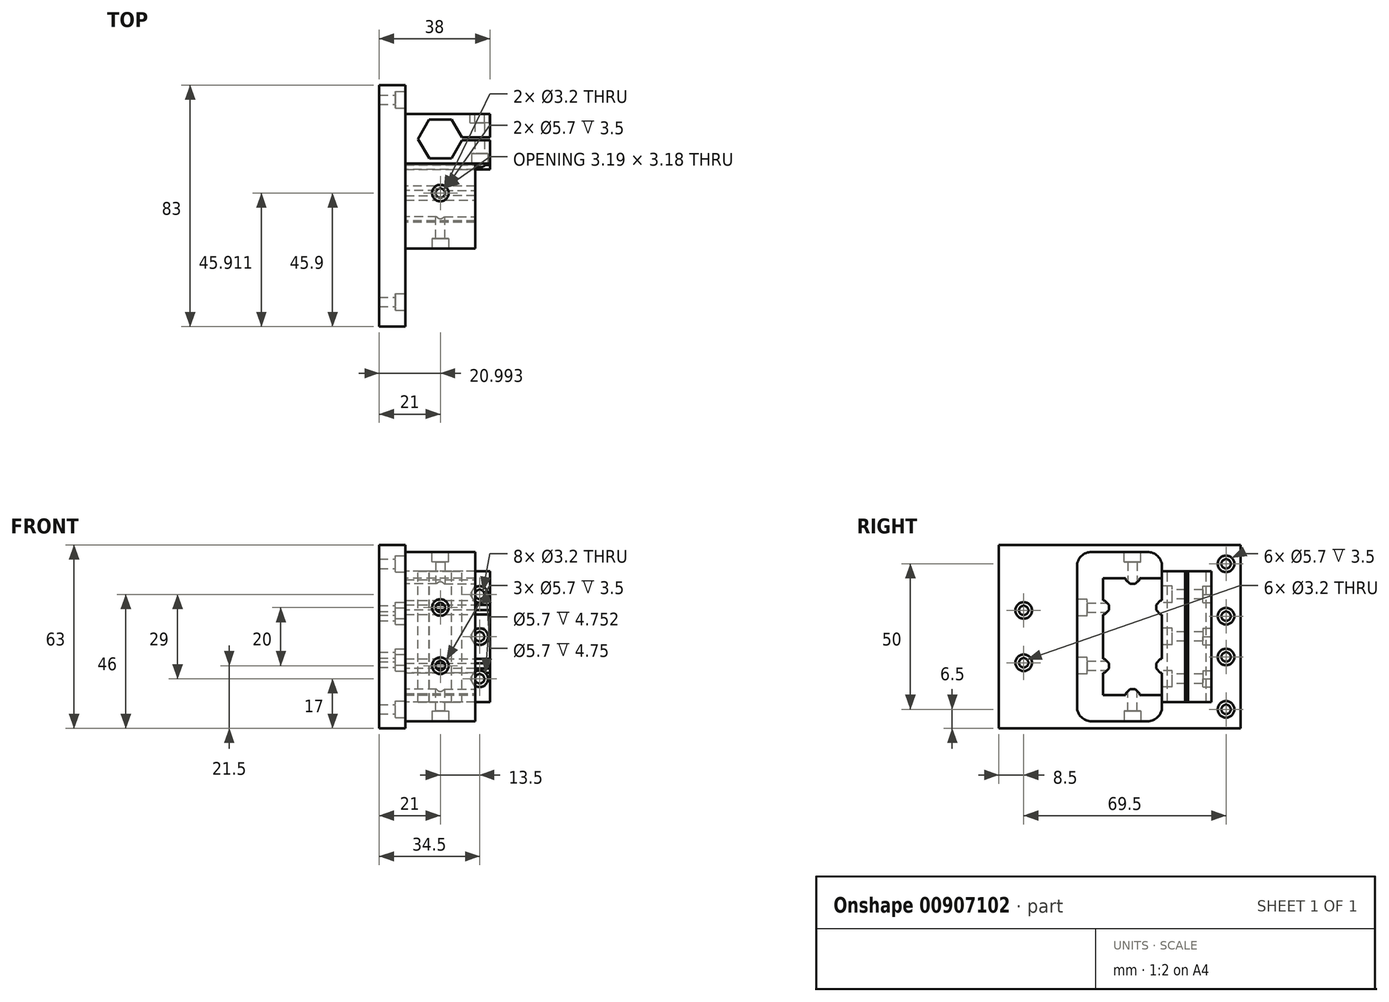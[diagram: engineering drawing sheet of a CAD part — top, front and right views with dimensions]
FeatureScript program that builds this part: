
annotation { "Feature Type Name" : "Feature", "Feature Type Description" : "" }
export const myFeature = defineFeature(function(context is Context, id is Id, definition is map)
    precondition{}
    {
        {
            assignVariable(context, id + "F0", {"name" : "headdepth", "anyValue" : 3.5 * mm});
        }
        {
            assignVariable(context, id + "F1", {"name" : "nutdepth", "anyValue" : 3});
        }
        {
            var Q0;
            Q0=qCreatedBy(makeId("Top.planeOp"),FACE);
            var sketch = newSketch(context, id + "F2", { "sketchPlane" : qUnion([Q0])});
            skLineSegment(sketch, "E0.bottom", {"start": v(0, 0) * mm, "end": v(9, 0) * mm});
            skLineSegment(sketch, "E0.top", {"start": v(0, 83) * mm, "end": v(9, 83) * mm});
            skLineSegment(sketch, "E0.left", {"start": v(0, 0) * mm, "end": v(0, 83) * mm});
            skLineSegment(sketch, "E0.right", {"start": v(9, 0) * mm, "end": v(9, 83) * mm});
            skSolve(sketch);
        }
        {
            var Q0;
            Q0 = qSketchRegion(id + "F2", true);
            var Q1;
            Q1=makeQuery(id+"F2.imprint","IMPRINT",FACE,{"disambiguationData":[TD([[makeQuery(id+"F2.imprint","IMPRINT",EDGE,{"derivedFrom":sQuery(id+"F2.wireOp",EDGE,"E0.bottom")}),1.0]])]});
            extrude(context, id + "F3", {"entities" : qUnion([Q0, Q1]), "depth" : 63 * mm, "offsetDistance" : 25 * mm});
        }
        {
            var Q0;
            Q0=makeQuery(id+"F3.opExtrude","SWEPT_FACE",FACE,{"disambiguationData":[OSD([sQuery(id+"F2.wireOp",EDGE,"E0.right")])]});
            var sketch = newSketch(context, id + "F4", { "sketchPlane" : qUnion([Q0])});
            skLineSegment(sketch, "E1", {"start": v(83, 6.5) * mm, "end": v(0, 6.5) * mm, "construction": true});
            skLineSegment(sketch, "E2", {"start": v(0, 24.5) * mm, "end": v(83, 24.5) * mm, "construction": true});
            skLineSegment(sketch, "E3", {"start": v(83, 38.5) * mm, "end": v(0, 38.5) * mm, "construction": true});
            skLineSegment(sketch, "E4", {"start": v(0, 56.5) * mm, "end": v(83, 56.5) * mm, "construction": true});
            skLineSegment(sketch, "E5", {"start": v(78, 63) * mm, "end": v(78, 0) * mm, "construction": true});
            skLineSegment(sketch, "E6", {"start": v(8.5, 63) * mm, "end": v(8.5, 0) * mm, "construction": true});
            skLineSegment(sketch, "E7", {"start": v(0, 22.5) * mm, "end": v(8.5, 22.5) * mm, "construction": true});
            skLineSegment(sketch, "E8", {"start": v(0, 40.5) * mm, "end": v(8.5, 40.5) * mm, "construction": true});
            skCircle(sketch, "E9", {"center": v(8.5, 40.5) * mm, "radius": 2.85 * mm});
            skCircle(sketch, "E10", {"center": v(8.5, 22.5) * mm, "radius": 2.85 * mm});
            skCircle(sketch, "E11", {"center": v(78, 56.5) * mm, "radius": 2.85 * mm});
            skCircle(sketch, "E12", {"center": v(78, 38.5) * mm, "radius": 2.85 * mm});
            skCircle(sketch, "E13", {"center": v(78, 24.5) * mm, "radius": 2.85 * mm});
            skCircle(sketch, "E14", {"center": v(78, 6.5) * mm, "radius": 2.85 * mm});
            skSolve(sketch);
        }
        {
            var Q0;
            Q0 = qSketchRegion(id + "F4", true);
            var Q1;
            Q1=makeQuery(id+"F4.imprint","IMPRINT",FACE,{"disambiguationData":[TD([[makeQuery(id+"F4.imprint","IMPRINT",EDGE,{"derivedFrom":sQuery(id+"F4.wireOp",EDGE,"E9")}),1.0]])]});
            extrude(context, id + "F5", {"entities" : qUnion([Q0, Q1]), "operationType" : NewBodyOperationType.REMOVE, "oppositeDirection" : true, "depth" : getVariable(context, 'headdepth'), "offsetDistance" : 25 * mm});
        }
        {
            var Q0;
            Q0=makeQuery(id+"F4.imprint","IMPRINT",FACE,{"disambiguationData":[TD([[makeQuery(id+"F4.imprint","IMPRINT",EDGE,{"derivedFrom":sQuery(id+"F4.wireOp",EDGE,"E9")}),1.0]])]});
            var sketch = newSketch(context, id + "F6", { "sketchPlane" : qUnion([Q0])});
            skCircle(sketch, "E15", {"center": v(8.5, 40.5) * mm, "radius": 1.6 * mm});
            skCircle(sketch, "E16", {"center": v(8.5, 22.5) * mm, "radius": 1.6 * mm});
            skCircle(sketch, "E17", {"center": v(78, 24.5) * mm, "radius": 1.6 * mm});
            skCircle(sketch, "E18", {"center": v(78, 38.5) * mm, "radius": 1.6 * mm});
            skCircle(sketch, "E19", {"center": v(78, 56.5) * mm, "radius": 1.6 * mm});
            skCircle(sketch, "E20", {"center": v(78, 6.5) * mm, "radius": 1.6 * mm});
            skSolve(sketch);
        }
        {
            var Q0;
            Q0 = qSketchRegion(id + "F6", true);
            extrude(context, id + "F7", {"entities" : qUnion([Q0]), "operationType" : NewBodyOperationType.REMOVE, "oppositeDirection" : true, "depth" : 25 * mm, "offsetDistance" : 25 * mm});
        }
        {
            var Q0;
            Q0=makeQuery(id+"F4.imprint","IMPRINT",FACE,{"disambiguationData":[TD([[makeQuery(id+"F4.imprint","IMPRINT",EDGE,{"derivedFrom":sQuery(id+"F4.wireOp",EDGE,"E9")}),-1.0]])]});
            var sketch = newSketch(context, id + "F8", { "sketchPlane" : qUnion([Q0])});
            skLineSegment(sketch, "E21", {"start": v(64.5, 0) * mm, "end": v(64.5, 79.23) * mm, "construction": true});
            skLineSegment(sketch, "E22", {"start": v(0, 31.5) * mm, "end": v(82.89, 31.5) * mm, "construction": true});
            skLineSegment(sketch, "E23", {"start": v(0, 54) * mm, "end": v(83.05, 54) * mm, "construction": true});
            skLineSegment(sketch, "E24", {"start": v(0, 9) * mm, "end": v(83.14, 9) * mm, "construction": true});
            skLineSegment(sketch, "E25", {"start": v(56, 9) * mm, "end": v(56, 54) * mm});
            skLineSegment(sketch, "E26", {"start": v(73, 54) * mm, "end": v(73, 9) * mm});
            skLineSegment(sketch, "E27", {"start": v(56, 54) * mm, "end": v(73, 54) * mm});
            skLineSegment(sketch, "E28", {"start": v(73, 9) * mm, "end": v(56, 9) * mm});
            skLineSegment(sketch, "E29", {"start": v(56, 9) * mm, "end": v(56, 0) * mm, "construction": true});
            skLineSegment(sketch, "E30", {"start": v(56, 54) * mm, "end": v(56, 64.2) * mm, "construction": true});
            skSolve(sketch);
        }
        {
            var Q0;
            Q0 = qSketchRegion(id + "F8", true);
            var Q1;
            Q1=makeQuery(id+"F8.imprint","IMPRINT",FACE,{"disambiguationData":[TD([[makeQuery(id+"F8.imprint","IMPRINT",EDGE,{"derivedFrom":sQuery(id+"F8.wireOp",EDGE,"E25")}),-1.0]])]});
            extrude(context, id + "F9", {"entities" : qUnion([Q0, Q1]), "operationType" : NewBodyOperationType.ADD, "depth" : 20 * mm, "offsetDistance" : 25 * mm});
        }
        {
            var Q0;
            Q0=makeQuery(id+"F9.opExtrude","SWEPT_FACE",FACE,{"disambiguationData":[OSD([sQuery(id+"F8.wireOp",EDGE,"E27")])]});
            var sketch = newSketch(context, id + "F10", { "sketchPlane" : qUnion([Q0])});
            skCircle(sketch, "E31.cCircle", {"center": v(21, 64.5) * mm, "radius": 6.65 * mm, "construction": true});
            skLineSegment(sketch, "E31.0", {"start": v(24.8, 71.17) * mm, "end": v(28.68, 64.55) * mm});
            skLineSegment(sketch, "E31.1", {"start": v(28.68, 64.55) * mm, "end": v(24.88, 57.87) * mm});
            skLineSegment(sketch, "E31.2", {"start": v(24.88, 57.87) * mm, "end": v(17.2, 57.83) * mm});
            skLineSegment(sketch, "E31.3", {"start": v(17.2, 57.83) * mm, "end": v(13.32, 64.45) * mm});
            skLineSegment(sketch, "E31.4", {"start": v(13.32, 64.45) * mm, "end": v(17.12, 71.13) * mm});
            skLineSegment(sketch, "E31.5", {"start": v(17.12, 71.13) * mm, "end": v(24.8, 71.17) * mm});
            skPoint(sketch, "E31.0.midPoint", {"position": v(26.74, 67.86) * mm});
            skLineSegment(sketch, "E32", {"start": v(21, 73) * mm, "end": v(21, 56) * mm, "construction": true});
            skLineSegment(sketch, "E33", {"start": v(9, 64.5) * mm, "end": v(29, 64.5) * mm, "construction": true});
            skSolve(sketch);
        }
        {
            var Q0;
            Q0 = qSketchRegion(id + "F10", true);
            var Q1;
            Q1=makeQuery(id+"F10.imprint","IMPRINT",FACE,{"disambiguationData":[TD([[makeQuery(id+"F10.imprint","IMPRINT",EDGE,{"derivedFrom":sQuery(id+"F10.wireOp",EDGE,"E31.0")}),-1.0]])]});
            extrude(context, id + "F11", {"entities" : qUnion([Q0, Q1]), "operationType" : NewBodyOperationType.REMOVE, "oppositeDirection" : true, "depth" : 70 * mm, "offsetDistance" : 25 * mm});
        }
        {
            var Q0;
            Q0=makeQuery(id+"F9.opExtrude","CAP_FACE",FACE,{"disambiguationData":[OSD([sQuery(id+"F8.wireOp",EDGE,"E25"),sQuery(id+"F8.wireOp",EDGE,"E26"),sQuery(id+"F8.wireOp",EDGE,"E27"),sQuery(id+"F8.wireOp",EDGE,"E28")])],"isStart":false});
            var sketch = newSketch(context, id + "F12", { "sketchPlane" : qUnion([Q0])});
            skLineSegment(sketch, "E34", {"start": v(64.5, 54) * mm, "end": v(64.5, 9) * mm, "construction": true});
            skLineSegment(sketch, "E35", {"start": v(65, 54) * mm, "end": v(65, 9) * mm});
            skLineSegment(sketch, "E36", {"start": v(64, 54) * mm, "end": v(64, 9) * mm});
            skSolve(sketch);
        }
        {
            var Q0;
            Q0 = qSketchRegion(id + "F12", true);
            var Q1;
            {var subQ0=sQuery(id+"F12.wireOp",EDGE,"E35");Q1=makeQuery(id+"F12.imprint","IMPRINT",FACE,{"disambiguationData":[TD([[makeQuery(id+"F12.imprint","IMPRINT",EDGE,{"derivedFrom":subQ0}),1.0]])]});}
            var Q2;
            {var subQ0=sQuery(id+"F12.wireOp",EDGE,"E36");Q2=makeQuery(id+"F12.imprint","IMPRINT",FACE,{"disambiguationData":[TD([[makeQuery(id+"F12.imprint","IMPRINT",EDGE,{"derivedFrom":subQ0}),-1.0]])]});}
            extrude(context, id + "F13", {"entities" : qUnion([Q0, Q1, Q2]), "operationType" : NewBodyOperationType.ADD, "depth" : 9 * mm, "offsetDistance" : 25 * mm});
        }
        {
            var Q0;
            Q0 = qSketchRegion(id + "F12", true);
            var Q1;
            Q1=makeQuery(id+"F9.opExtrude","CAP_FACE",FACE,{"disambiguationData":[OSD([sQuery(id+"F8.wireOp",EDGE,"E25"),sQuery(id+"F8.wireOp",EDGE,"E26"),sQuery(id+"F8.wireOp",EDGE,"E27"),sQuery(id+"F8.wireOp",EDGE,"E28")])],"isStart":false});
            extrude(context, id + "F14", {"entities" : qUnion([Q0, Q1]), "operationType" : NewBodyOperationType.REMOVE, "oppositeDirection" : true, "depth" : 5 * mm, "offsetDistance" : 25 * mm});
        }
        {
            var Q0;
            {var subQ0=sQuery(id+"F8.wireOp",EDGE,"E25");Q0=makeQuery(id+"F13.boolean.opBoolean","MERGE",FACE,{"derivedFrom":[makeQuery(id+"F9.opExtrude","SWEPT_FACE",FACE,{"disambiguationData":[OSD([subQ0])]}),makeQuery(id+"F13.opExtrude","SWEPT_FACE",FACE,{"disambiguationData":[OSD([subQ0])]})]});}
            var sketch = newSketch(context, id + "F15", { "sketchPlane" : qUnion([Q0])});
            skLineSegment(sketch, "E37", {"start": v(34.5, 54) * mm, "end": v(34.5, 9) * mm, "construction": true});
            skLineSegment(sketch, "E38", {"start": v(34.5, 46) * mm, "end": v(38, 46) * mm, "construction": true});
            skLineSegment(sketch, "E39.1.0.0", {"start": v(34.5, 31.5) * mm, "end": v(38, 31.5) * mm, "construction": true});
            skLineSegment(sketch, "E39.2.0.0", {"start": v(34.5, 17) * mm, "end": v(38, 17) * mm, "construction": true});
            skLineSegment(sketch, "E39.direction1", {"start": v(34.5, 46) * mm, "end": v(34.5, 31.5) * mm, "construction": true});
            skCircle(sketch, "E40", {"center": v(34.5, 46) * mm, "radius": 2.85 * mm});
            skCircle(sketch, "E41", {"center": v(34.5, 31.5) * mm, "radius": 2.85 * mm});
            skCircle(sketch, "E42", {"center": v(34.5, 17) * mm, "radius": 2.85 * mm});
            skSolve(sketch);
        }
        {
            var Q0;
            Q0 = qSketchRegion(id + "F15", true);
            extrude(context, id + "F16", {"entities" : qUnion([Q0]), "operationType" : NewBodyOperationType.REMOVE, "oppositeDirection" : true, "depth" : getVariable(context, 'headdepth'), "offsetDistance" : 25 * mm});
        }
        {
            var Q0;
            Q0=makeQuery(id+"F16.boolean.opBoolean","COPY",FACE,{"derivedFrom":makeQuery(id+"F16.opExtrude","CAP_FACE",FACE,{"disambiguationData":[OSD([sQuery(id+"F15.wireOp",EDGE,"E40")])],"isStart":false})});
            var sketch = newSketch(context, id + "F17", { "sketchPlane" : qUnion([Q0])});
            skCircle(sketch, "E43", {"center": v(34.5, 46) * mm, "radius": 1.6 * mm});
            skCircle(sketch, "E44", {"center": v(34.5, 31.5) * mm, "radius": 1.6 * mm});
            skCircle(sketch, "E45", {"center": v(34.5, 17) * mm, "radius": 1.6 * mm});
            skSolve(sketch);
        }
        {
            var Q0;
            Q0 = qSketchRegion(id + "F17", true);
            extrude(context, id + "F18", {"entities" : qUnion([Q0]), "operationType" : NewBodyOperationType.REMOVE, "oppositeDirection" : true, "depth" : 25 * mm, "offsetDistance" : 25 * mm});
        }
        {
            var Q0;
            {var subQ0=sQuery(id+"F8.wireOp",EDGE,"E26");Q0=makeQuery(id+"F13.boolean.opBoolean","MERGE",FACE,{"derivedFrom":[makeQuery(id+"F9.opExtrude","SWEPT_FACE",FACE,{"disambiguationData":[OSD([subQ0])]}),makeQuery(id+"F13.opExtrude","SWEPT_FACE",FACE,{"disambiguationData":[OSD([subQ0])]})]});}
            var sketch = newSketch(context, id + "F19", { "sketchPlane" : qUnion([Q0])});
            skCircle(sketch, "E46.cCircle", {"center": v(-34.5, 46) * mm, "radius": 2.85 * mm, "construction": true});
            skLineSegment(sketch, "E46.0", {"start": v(-36.15, 48.85) * mm, "end": v(-32.85, 48.85) * mm});
            skLineSegment(sketch, "E46.1", {"start": v(-32.85, 48.85) * mm, "end": v(-31.2, 46) * mm});
            skLineSegment(sketch, "E46.2", {"start": v(-31.2, 46) * mm, "end": v(-32.85, 43.15) * mm});
            skLineSegment(sketch, "E46.3", {"start": v(-32.85, 43.15) * mm, "end": v(-36.15, 43.15) * mm});
            skLineSegment(sketch, "E46.4", {"start": v(-36.15, 43.15) * mm, "end": v(-37.8, 46) * mm});
            skLineSegment(sketch, "E46.5", {"start": v(-37.8, 46) * mm, "end": v(-36.15, 48.85) * mm});
            skPoint(sketch, "E46.0.midPoint", {"position": v(-34.5, 48.85) * mm});
            skCircle(sketch, "E47.cCircle", {"center": v(-34.5, 31.5) * mm, "radius": 2.85 * mm, "construction": true});
            skLineSegment(sketch, "E47.0", {"start": v(-36.15, 28.65) * mm, "end": v(-37.8, 31.5) * mm});
            skLineSegment(sketch, "E47.1", {"start": v(-37.8, 31.5) * mm, "end": v(-36.15, 34.35) * mm});
            skLineSegment(sketch, "E47.2", {"start": v(-36.15, 34.35) * mm, "end": v(-32.85, 34.35) * mm});
            skLineSegment(sketch, "E47.3", {"start": v(-32.85, 34.35) * mm, "end": v(-31.2, 31.5) * mm});
            skLineSegment(sketch, "E47.4", {"start": v(-31.2, 31.5) * mm, "end": v(-32.85, 28.65) * mm});
            skLineSegment(sketch, "E47.5", {"start": v(-32.85, 28.65) * mm, "end": v(-36.15, 28.65) * mm});
            skPoint(sketch, "E47.0.midPoint", {"position": v(-36.97, 30.07) * mm});
            skCircle(sketch, "E48.cCircle", {"center": v(-34.5, 17) * mm, "radius": 2.85 * mm, "construction": true});
            skLineSegment(sketch, "E48.0", {"start": v(-32.85, 19.85) * mm, "end": v(-31.2, 17) * mm});
            skLineSegment(sketch, "E48.1", {"start": v(-31.2, 17) * mm, "end": v(-32.85, 14.15) * mm});
            skLineSegment(sketch, "E48.2", {"start": v(-32.85, 14.15) * mm, "end": v(-36.15, 14.15) * mm});
            skLineSegment(sketch, "E48.3", {"start": v(-36.15, 14.15) * mm, "end": v(-37.8, 17) * mm});
            skLineSegment(sketch, "E48.4", {"start": v(-37.8, 17) * mm, "end": v(-36.15, 19.85) * mm});
            skLineSegment(sketch, "E48.5", {"start": v(-36.15, 19.85) * mm, "end": v(-32.85, 19.85) * mm});
            skPoint(sketch, "E48.0.midPoint", {"position": v(-32.03, 18.43) * mm});
            skSolve(sketch);
        }
        {
            var Q0;
            Q0 = qSketchRegion(id + "F19", true);
            extrude(context, id + "F20", {"entities" : qUnion([Q0]), "operationType" : NewBodyOperationType.REMOVE, "oppositeDirection" : true, "depth" : (getVariable(context, 'nutdepth')) * mm, "offsetDistance" : 25 * mm});
        }
        {
            var Q0;
            Q0=makeQuery(id+"F4.imprint","IMPRINT",FACE,{"disambiguationData":[TD([[makeQuery(id+"F4.imprint","IMPRINT",EDGE,{"derivedFrom":sQuery(id+"F4.wireOp",EDGE,"E9")}),-1.0]])]});
            var sketch = newSketch(context, id + "F21", { "sketchPlane" : qUnion([Q0])});
            skLineSegment(sketch, "E49", {"start": v(0, 51.6) * mm, "end": v(83, 51.6) * mm, "construction": true});
            skLineSegment(sketch, "E50", {"start": v(0, 11.4) * mm, "end": v(83, 11.4) * mm, "construction": true});
            skLineSegment(sketch, "E51", {"start": v(35.8, 51.6) * mm, "end": v(35.8, 11.4) * mm, "construction": true});
            skLineSegment(sketch, "E52.bottom", {"start": v(35.8, 51.6) * mm, "end": v(26.8, 51.6) * mm});
            skLineSegment(sketch, "E52.top", {"start": v(35.8, 11.4) * mm, "end": v(26.8, 11.4) * mm});
            skLineSegment(sketch, "E52.left", {"start": v(35.8, 51.6) * mm, "end": v(35.8, 11.4) * mm});
            skLineSegment(sketch, "E52.right", {"start": v(26.8, 51.6) * mm, "end": v(26.8, 11.4) * mm});
            skLineSegment(sketch, "E53.bottom", {"start": v(56, 2.4) * mm, "end": v(26.8, 2.4) * mm});
            skLineSegment(sketch, "E53.top", {"start": v(56, 11.4) * mm, "end": v(26.8, 11.4) * mm});
            skLineSegment(sketch, "E53.left", {"start": v(56, 2.4) * mm, "end": v(56, 11.4) * mm});
            skLineSegment(sketch, "E53.right", {"start": v(26.8, 2.4) * mm, "end": v(26.8, 11.4) * mm});
            skLineSegment(sketch, "E54.bottom", {"start": v(56, 51.6) * mm, "end": v(26.8, 51.6) * mm});
            skLineSegment(sketch, "E54.top", {"start": v(56, 60.6) * mm, "end": v(26.8, 60.6) * mm});
            skLineSegment(sketch, "E54.left", {"start": v(56, 51.6) * mm, "end": v(56, 60.6) * mm});
            skLineSegment(sketch, "E54.right", {"start": v(26.8, 51.6) * mm, "end": v(26.8, 60.6) * mm});
            skSolve(sketch);
        }
        {
            var Q0;
            {var subQ0=makeQuery(id+"F21.imprint","IMPRINT",EDGE,{"derivedFrom":sQuery(id+"F21.wireOp",EDGE,"E52.top")});var subQ1=makeQuery(id+"F21.imprint","IMPRINT",EDGE,{"derivedFrom":sQuery(id+"F21.wireOp",EDGE,"E52.bottom")});Q0=qUnion([makeQuery(id+"F21.imprint","IMPRINT",FACE,{"disambiguationData":[TD([[subQ1,1.0]])]}),makeQuery(id+"F21.imprint","IMPRINT",FACE,{"disambiguationData":[TD([[subQ1,-1.0]])]}),makeQuery(id+"F21.imprint","IMPRINT",FACE,{"disambiguationData":[TD([[subQ0,1.0]])]})]);}
            var Q1;
            Q1=makeQuery(id+"F21.imprint","IMPRINT",FACE,{"disambiguationData":[TD([[makeQuery(id+"F21.imprint","IMPRINT",EDGE,{"derivedFrom":sQuery(id+"F21.wireOp",EDGE,"E52.bottom")}),1.0]])]});
            extrude(context, id + "F22", {"entities" : qUnion([Q0, Q1]), "operationType" : NewBodyOperationType.ADD, "depth" : 24 * mm, "offsetDistance" : 25 * mm});
        }
        {
            var Q0;
            Q0=makeQuery(id+"F22.opExtrude","SWEPT_FACE",FACE,{"disambiguationData":[OSD([sQuery(id+"F21.wireOp",EDGE,"E52.left")])]});
            var sketch = newSketch(context, id + "F23", { "sketchPlane" : qUnion([Q0])});
            skLineSegment(sketch, "E55", {"start": v(-9, 31.5) * mm, "end": v(-33, 31.5) * mm, "construction": true});
            skLineSegment(sketch, "E56", {"start": v(-9, 41.5) * mm, "end": v(-33, 41.5) * mm, "construction": true});
            skLineSegment(sketch, "E57", {"start": v(-9, 21.5) * mm, "end": v(-33, 21.5) * mm, "construction": true});
            skLineSegment(sketch, "E58.bottom", {"start": v(-9, 43.9) * mm, "end": v(-33, 43.9) * mm});
            skLineSegment(sketch, "E58.top", {"start": v(-9, 39.1) * mm, "end": v(-33, 39.1) * mm});
            skLineSegment(sketch, "E58.left", {"start": v(-9, 43.9) * mm, "end": v(-9, 39.1) * mm});
            skLineSegment(sketch, "E58.right", {"start": v(-33, 43.9) * mm, "end": v(-33, 39.1) * mm});
            skLineSegment(sketch, "E59.bottom", {"start": v(-9, 23.9) * mm, "end": v(-33, 23.9) * mm});
            skLineSegment(sketch, "E59.top", {"start": v(-9, 19.1) * mm, "end": v(-33, 19.1) * mm});
            skLineSegment(sketch, "E59.left", {"start": v(-9, 23.9) * mm, "end": v(-9, 19.1) * mm});
            skLineSegment(sketch, "E59.right", {"start": v(-33, 23.9) * mm, "end": v(-33, 19.1) * mm});
            skSolve(sketch);
        }
        {
            var Q0;
            Q0 = qSketchRegion(id + "F23", true);
            extrude(context, id + "F24", {"entities" : qUnion([Q0]), "operationType" : NewBodyOperationType.ADD, "depth" : 2 * mm, "offsetDistance" : 25 * mm});
        }
        {
            var Q0;
            Q0=makeQuery(id+"F24.opExtrude","CAP_EDGE",EDGE,{"disambiguationData":[OSD([sQuery(id+"F23.wireOp",EDGE,"E58.top")])],"isStart":false});
            var Q1;
            Q1=makeQuery(id+"F24.opExtrude","CAP_EDGE",EDGE,{"disambiguationData":[OSD([sQuery(id+"F23.wireOp",EDGE,"E58.bottom")])],"isStart":false});
            var Q2;
            Q2=makeQuery(id+"F24.opExtrude","CAP_EDGE",EDGE,{"disambiguationData":[OSD([sQuery(id+"F23.wireOp",EDGE,"E59.bottom")])],"isStart":false});
            var Q3;
            Q3=makeQuery(id+"F24.opExtrude","CAP_EDGE",EDGE,{"disambiguationData":[OSD([sQuery(id+"F23.wireOp",EDGE,"E59.top")])],"isStart":false});
            chamfer(context, id + "F25", {"entities" : qUnion([Q0, Q1, Q2, Q3]), "width" : 1.5 * mm, "tangentPropagation" : true});
        }
        {
            var Q0;
            Q0=makeQuery(id+"F24.opExtrude","CAP_FACE",FACE,{"disambiguationData":[OSD([sQuery(id+"F23.wireOp",EDGE,"E58.bottom"),sQuery(id+"F23.wireOp",EDGE,"E58.top"),sQuery(id+"F23.wireOp",EDGE,"E58.left"),sQuery(id+"F23.wireOp",EDGE,"E58.right")])],"isStart":false});
            var sketch = newSketch(context, id + "F26", { "sketchPlane" : qUnion([Q0])});
            skLineSegment(sketch, "E60", {"start": v(-9, 41.5) * mm, "end": v(-33, 41.5) * mm, "construction": true});
            skLineSegment(sketch, "E61", {"start": v(-21, 42.4) * mm, "end": v(-21, 40.6) * mm, "construction": true});
            skCircle(sketch, "E62", {"center": v(-21, 41.5) * mm, "radius": 1.6 * mm});
            skSolve(sketch);
        }
        {
            var Q0;
            Q0 = qSketchRegion(id + "F26", true);
            var Q1;
            {var subQ0=sQuery(id+"F26.wireOp",EDGE,"E62");var subQ1=sQuery(id+"F23.wireOp",EDGE,"E58.top");var subQ2=sQuery(id+"F23.wireOp",EDGE,"E58.bottom");var subQ3=makeQuery(id+"F24.opExtrude","CAP_FACE",FACE,{"disambiguationData":[OSD([subQ2,subQ1,sQuery(id+"F23.wireOp",EDGE,"E58.left"),sQuery(id+"F23.wireOp",EDGE,"E58.right")])],"isStart":false});var subQ4=makeQuery(id+"F25.opChamfer","BLEND_EDGE",EDGE,{"blendedFrom":[makeQuery(id+"F24.opExtrude","CAP_EDGE",EDGE,{"disambiguationData":[OSD([subQ2])],"isStart":false}),subQ3],"blendedInto":[subQ3]});var subQ5=makeQuery(id+"F26.imprint","INTERSECT",VERTEX,{"disambiguationData":[OD(0.0)],"derivedFrom":[subQ4,subQ0]});Q1=makeQuery(id+"F26.imprint","IMPRINT",FACE,{"disambiguationData":[TD([[makeQuery(id+"F26.imprint","IMPRINT",EDGE,{"disambiguationData":[TD([[subQ5,-1.0]])],"derivedFrom":subQ0}),1.0]])]});}
            extrude(context, id + "F27", {"entities" : qUnion([Q0, Q1]), "operationType" : NewBodyOperationType.REMOVE, "oppositeDirection" : true, "depth" : 25 * mm, "offsetDistance" : 25 * mm});
        }
        {
            var Q0;
            Q0=makeQuery(id+"F24.opExtrude","CAP_FACE",FACE,{"disambiguationData":[OSD([sQuery(id+"F23.wireOp",EDGE,"E59.bottom"),sQuery(id+"F23.wireOp",EDGE,"E59.top"),sQuery(id+"F23.wireOp",EDGE,"E59.left"),sQuery(id+"F23.wireOp",EDGE,"E59.right")])],"isStart":false});
            var sketch = newSketch(context, id + "F28", { "sketchPlane" : qUnion([Q0])});
            skLineSegment(sketch, "E63", {"start": v(-9, 21.5) * mm, "end": v(-33, 21.5) * mm, "construction": true});
            skLineSegment(sketch, "E64", {"start": v(-21, 20.6) * mm, "end": v(-21, 22.4) * mm, "construction": true});
            skCircle(sketch, "E65", {"center": v(-21, 21.5) * mm, "radius": 1.6 * mm});
            skSolve(sketch);
        }
        {
            var Q0;
            Q0 = qSketchRegion(id + "F28", true);
            extrude(context, id + "F29", {"entities" : qUnion([Q0]), "operationType" : NewBodyOperationType.REMOVE, "oppositeDirection" : true, "depth" : 25 * mm, "offsetDistance" : 25 * mm});
        }
        {
            var Q0;
            Q0=makeQuery(id+"F15.imprint","IMPRINT",FACE,{"disambiguationData":[TD([[makeQuery(id+"F15.imprint","IMPRINT",EDGE,{"derivedFrom":sQuery(id+"F15.wireOp",EDGE,"E40")}),-1.0]])]});
            var sketch = newSketch(context, id + "F30", { "sketchPlane" : qUnion([Q0])});
            skLineSegment(sketch, "E66", {"start": v(9, 41.5) * mm, "end": v(38, 41.5) * mm, "construction": true});
            skLineSegment(sketch, "E67", {"start": v(38, 21.5) * mm, "end": v(9, 21.5) * mm, "construction": true});
            skLineSegment(sketch, "E68.bottom", {"start": v(9, 23.9) * mm, "end": v(38, 23.9) * mm});
            skLineSegment(sketch, "E68.top", {"start": v(9, 19.1) * mm, "end": v(38, 19.1) * mm});
            skLineSegment(sketch, "E68.left", {"start": v(9, 23.9) * mm, "end": v(9, 19.1) * mm});
            skLineSegment(sketch, "E68.right", {"start": v(38, 23.9) * mm, "end": v(38, 19.1) * mm});
            skLineSegment(sketch, "E69.bottom", {"start": v(9, 43.9) * mm, "end": v(38, 43.9) * mm});
            skLineSegment(sketch, "E69.top", {"start": v(9, 39.1) * mm, "end": v(38, 39.1) * mm});
            skLineSegment(sketch, "E69.left", {"start": v(9, 43.9) * mm, "end": v(9, 39.1) * mm});
            skLineSegment(sketch, "E69.right", {"start": v(38, 43.9) * mm, "end": v(38, 39.1) * mm});
            skSolve(sketch);
        }
        {
            var Q0;
            Q0 = qSketchRegion(id + "F30", true);
            extrude(context, id + "F31", {"entities" : qUnion([Q0]), "operationType" : NewBodyOperationType.ADD, "depth" : 2 * mm, "offsetDistance" : 25 * mm});
        }
        {
            var Q0;
            Q0=makeQuery(id+"F31.opExtrude","CAP_EDGE",EDGE,{"disambiguationData":[OSD([sQuery(id+"F30.wireOp",EDGE,"E69.bottom")])],"isStart":false});
            var Q1;
            Q1=makeQuery(id+"F31.opExtrude","CAP_EDGE",EDGE,{"disambiguationData":[OSD([sQuery(id+"F30.wireOp",EDGE,"E69.top")])],"isStart":false});
            var Q2;
            Q2=makeQuery(id+"F31.opExtrude","CAP_EDGE",EDGE,{"disambiguationData":[OSD([sQuery(id+"F30.wireOp",EDGE,"E68.bottom")])],"isStart":false});
            var Q3;
            Q3=makeQuery(id+"F31.opExtrude","CAP_EDGE",EDGE,{"disambiguationData":[OSD([sQuery(id+"F30.wireOp",EDGE,"E68.top")])],"isStart":false});
            chamfer(context, id + "F32", {"entities" : qUnion([Q0, Q1, Q2, Q3]), "width" : 1.5 * mm, "tangentPropagation" : true});
        }
        {
            var Q0;
            Q0 = qSketchRegion(id + "F15", true);
            extrude(context, id + "F33", {"entities" : qUnion([Q0]), "operationType" : NewBodyOperationType.REMOVE, "depth" : 3 * mm, "offsetDistance" : 25 * mm});
        }
        {
            var Q0;
            Q0=makeQuery(id+"F22.opExtrude","SWEPT_FACE",FACE,{"disambiguationData":[OSD([sQuery(id+"F21.wireOp",EDGE,"E54.bottom")])]});
            var sketch = newSketch(context, id + "F34", { "sketchPlane" : qUnion([Q0])});
            skLineSegment(sketch, "E70", {"start": v(9, -45.9) * mm, "end": v(33, -45.9) * mm, "construction": true});
            skLineSegment(sketch, "E71.bottom", {"start": v(33, -43.5) * mm, "end": v(9, -43.5) * mm});
            skLineSegment(sketch, "E71.top", {"start": v(33, -48.3) * mm, "end": v(9, -48.3) * mm});
            skLineSegment(sketch, "E71.left", {"start": v(33, -43.5) * mm, "end": v(33, -48.3) * mm});
            skLineSegment(sketch, "E71.right", {"start": v(9, -43.5) * mm, "end": v(9, -48.3) * mm});
            skSolve(sketch);
        }
        {
            var Q0;
            Q0 = qSketchRegion(id + "F34", true);
            extrude(context, id + "F35", {"entities" : qUnion([Q0]), "operationType" : NewBodyOperationType.ADD, "depth" : 2 * mm, "offsetDistance" : 25 * mm});
        }
        {
            var Q0;
            Q0=makeQuery(id+"F35.opExtrude","CAP_EDGE",EDGE,{"disambiguationData":[OSD([sQuery(id+"F34.wireOp",EDGE,"E71.bottom")])],"isStart":false});
            var Q1;
            Q1=makeQuery(id+"F35.opExtrude","CAP_EDGE",EDGE,{"disambiguationData":[OSD([sQuery(id+"F34.wireOp",EDGE,"E71.top")])],"isStart":false});
            chamfer(context, id + "F36", {"entities" : qUnion([Q0, Q1]), "width" : 1.5 * mm, "tangentPropagation" : true});
        }
        {
            var Q0;
            Q0=makeQuery(id+"F35.opExtrude","CAP_FACE",FACE,{"disambiguationData":[OSD([sQuery(id+"F34.wireOp",EDGE,"E71.bottom"),sQuery(id+"F34.wireOp",EDGE,"E71.top"),sQuery(id+"F34.wireOp",EDGE,"E71.left"),sQuery(id+"F34.wireOp",EDGE,"E71.right")])],"isStart":false});
            var sketch = newSketch(context, id + "F37", { "sketchPlane" : qUnion([Q0])});
            skLineSegment(sketch, "E72", {"start": v(33, -45.9) * mm, "end": v(9, -45.9) * mm, "construction": true});
            skLineSegment(sketch, "E73", {"start": v(21, -45) * mm, "end": v(21, -46.8) * mm, "construction": true});
            skCircle(sketch, "E74", {"center": v(21, -45.9) * mm, "radius": 1.6 * mm});
            skSolve(sketch);
        }
        {
            var Q0;
            Q0 = qSketchRegion(id + "F37", true);
            extrude(context, id + "F38", {"entities" : qUnion([Q0]), "operationType" : NewBodyOperationType.REMOVE, "oppositeDirection" : true, "depth" : 25 * mm, "offsetDistance" : 25 * mm});
        }
        {
            var Q0;
            Q0=makeQuery(id+"F22.opExtrude","SWEPT_FACE",FACE,{"disambiguationData":[OSD([sQuery(id+"F21.wireOp",EDGE,"E53.top")])]});
            var sketch = newSketch(context, id + "F39", { "sketchPlane" : qUnion([Q0])});
            skLineSegment(sketch, "E75", {"start": v(9, 45.9) * mm, "end": v(33, 45.9) * mm, "construction": true});
            skLineSegment(sketch, "E76.bottom", {"start": v(9, 48.3) * mm, "end": v(33, 48.3) * mm});
            skLineSegment(sketch, "E76.top", {"start": v(9, 43.5) * mm, "end": v(33, 43.5) * mm});
            skLineSegment(sketch, "E76.left", {"start": v(9, 48.3) * mm, "end": v(9, 43.5) * mm});
            skLineSegment(sketch, "E76.right", {"start": v(33, 48.3) * mm, "end": v(33, 43.5) * mm});
            skSolve(sketch);
        }
        {
            var Q0;
            Q0 = qSketchRegion(id + "F39", true);
            extrude(context, id + "F40", {"entities" : qUnion([Q0]), "operationType" : NewBodyOperationType.ADD, "depth" : 2 * mm, "offsetDistance" : 25 * mm});
        }
        {
            var Q0;
            Q0=makeQuery(id+"F40.opExtrude","CAP_EDGE",EDGE,{"disambiguationData":[OSD([sQuery(id+"F39.wireOp",EDGE,"E76.bottom")])],"isStart":false});
            var Q1;
            Q1=makeQuery(id+"F40.opExtrude","CAP_EDGE",EDGE,{"disambiguationData":[OSD([sQuery(id+"F39.wireOp",EDGE,"E76.top")])],"isStart":false});
            chamfer(context, id + "F41", {"entities" : qUnion([Q0, Q1]), "width" : 1.5 * mm, "tangentPropagation" : true});
        }
        {
            var Q0;
            Q0=makeQuery(id+"F40.opExtrude","CAP_FACE",FACE,{"disambiguationData":[OSD([sQuery(id+"F39.wireOp",EDGE,"E76.bottom"),sQuery(id+"F39.wireOp",EDGE,"E76.top"),sQuery(id+"F39.wireOp",EDGE,"E76.left"),sQuery(id+"F39.wireOp",EDGE,"E76.right")])],"isStart":false});
            var sketch = newSketch(context, id + "F42", { "sketchPlane" : qUnion([Q0])});
            skLineSegment(sketch, "E77", {"start": v(33, 45.9) * mm, "end": v(9, 45.9) * mm, "construction": true});
            skLineSegment(sketch, "E78", {"start": v(21, 46.8) * mm, "end": v(21, 45) * mm, "construction": true});
            skCircle(sketch, "E79", {"center": v(21, 45.9) * mm, "radius": 1.6 * mm});
            skSolve(sketch);
        }
        {
            var Q0;
            Q0 = qSketchRegion(id + "F42", true);
            extrude(context, id + "F43", {"entities" : qUnion([Q0]), "operationType" : NewBodyOperationType.REMOVE, "oppositeDirection" : true, "depth" : 25 * mm, "offsetDistance" : 25 * mm});
        }
        {
            var Q0;
            Q0=makeQuery(id+"F22.opExtrude","SWEPT_FACE",FACE,{"disambiguationData":[OSD([sQuery(id+"F21.wireOp",EDGE,"E53.bottom")])]});
            var sketch = newSketch(context, id + "F44", { "sketchPlane" : qUnion([Q0])});
            skLineSegment(sketch, "E80", {"start": v(22.6, -45.9) * mm, "end": v(19.4, -45.9) * mm, "construction": true});
            skLineSegment(sketch, "E81", {"start": v(21, -47.5) * mm, "end": v(21, -44.3) * mm, "construction": true});
            skCircle(sketch, "E82", {"center": v(21, -45.9) * mm, "radius": 2.85 * mm});
            skSolve(sketch);
        }
        {
            var Q0;
            Q0 = qSketchRegion(id + "F44", true);
            extrude(context, id + "F45", {"entities" : qUnion([Q0]), "operationType" : NewBodyOperationType.REMOVE, "oppositeDirection" : true, "depth" : getVariable(context, 'headdepth'), "offsetDistance" : 25 * mm});
        }
        {
            var Q0;
            Q0=makeQuery(id+"F22.opExtrude","SWEPT_FACE",FACE,{"disambiguationData":[OSD([sQuery(id+"F21.wireOp",EDGE,"E52.right"),sQuery(id+"F21.wireOp",EDGE,"E53.right"),sQuery(id+"F21.wireOp",EDGE,"E54.right")])]});
            var sketch = newSketch(context, id + "F46", { "sketchPlane" : qUnion([Q0])});
            skLineSegment(sketch, "E83", {"start": v(21, 43.1) * mm, "end": v(21, 39.9) * mm, "construction": true});
            skLineSegment(sketch, "E84", {"start": v(19.4, 41.5) * mm, "end": v(22.6, 41.5) * mm, "construction": true});
            skCircle(sketch, "E85", {"center": v(21, 41.5) * mm, "radius": 2.85 * mm});
            skLineSegment(sketch, "E86", {"start": v(21, 23.1) * mm, "end": v(21, 19.9) * mm, "construction": true});
            skLineSegment(sketch, "E87", {"start": v(19.4, 21.5) * mm, "end": v(22.6, 21.5) * mm, "construction": true});
            skCircle(sketch, "E88", {"center": v(21, 21.5) * mm, "radius": 2.85 * mm});
            skSolve(sketch);
        }
        {
            var Q0;
            Q0 = qSketchRegion(id + "F46", true);
            extrude(context, id + "F47", {"entities" : qUnion([Q0]), "operationType" : NewBodyOperationType.REMOVE, "oppositeDirection" : true, "depth" : getVariable(context, 'headdepth'), "offsetDistance" : 25 * mm});
        }
        {
            var Q0;
            Q0=makeQuery(id+"F22.opExtrude","SWEPT_EDGE",EDGE,{"disambiguationData":[OSD([sQuery(id+"F21.wireOp",EDGE,"E53.bottom"),sQuery(id+"F21.wireOp",EDGE,"E53.right")])]});
            fillet(context, id + "F48", {"entities" : qUnion([Q0]), "radius" : 5 * mm, "tangentPropagation" : true, "allowEdgeOverflow" : false});
        }
        {
            var Q0;
            Q0=makeQuery(id+"F22.opExtrude","SWEPT_EDGE",EDGE,{"disambiguationData":[OSD([sQuery(id+"F21.wireOp",EDGE,"E54.top"),sQuery(id+"F21.wireOp",EDGE,"E54.right")])]});
            fillet(context, id + "F49", {"entities" : qUnion([Q0]), "radius" : 5 * mm, "tangentPropagation" : true, "allowEdgeOverflow" : false});
        }
        {
            var Q0;
            Q0=makeQuery(id+"F22.opExtrude","SWEPT_EDGE",EDGE,{"disambiguationData":[OSD([sQuery(id+"F21.wireOp",EDGE,"E53.bottom"),sQuery(id+"F21.wireOp",EDGE,"E53.left")])]});
            var Q1;
            Q1=makeQuery(id+"F22.opExtrude","SWEPT_EDGE",EDGE,{"disambiguationData":[OSD([sQuery(id+"F21.wireOp",EDGE,"E54.top"),sQuery(id+"F21.wireOp",EDGE,"E54.left")])]});
            fillet(context, id + "F50", {"entities" : qUnion([Q0, Q1]), "radius" : 5 * mm, "tangentPropagation" : true, "allowEdgeOverflow" : false});
        }
        {
            var Q0;
            Q0=makeQuery(id+"F22.opExtrude","SWEPT_FACE",FACE,{"disambiguationData":[OSD([sQuery(id+"F21.wireOp",EDGE,"E54.top")])]});
            var sketch = newSketch(context, id + "F51", { "sketchPlane" : qUnion([Q0])});
            skLineSegment(sketch, "E89", {"start": v(22.6, 45.9) * mm, "end": v(19.4, 45.9) * mm, "construction": true});
            skLineSegment(sketch, "E90", {"start": v(21, 47.5) * mm, "end": v(21, 44.3) * mm, "construction": true});
            skCircle(sketch, "E91", {"center": v(21, 45.9) * mm, "radius": 2.85 * mm});
            skSolve(sketch);
        }
        {
            var Q0;
            Q0=makeQuery(id+"F51.imprint","IMPRINT",FACE,{"disambiguationData":[TD([[makeQuery(id+"F51.imprint","IMPRINT",EDGE,{"derivedFrom":makeQuery(id+"F38.boolean.opBoolean","INTERSECT",EDGE,{"derivedFrom":[makeQuery(id+"F22.opExtrude","SWEPT_FACE",FACE,{"disambiguationData":[OSD([sQuery(id+"F21.wireOp",EDGE,"E54.top")])]}),makeQuery(id+"F38.opExtrude","SWEPT_FACE",FACE,{"disambiguationData":[OSD([sQuery(id+"F37.wireOp",EDGE,"E74")])]})]})}),-1.0]])]});
            var Q1;
            Q1=makeQuery(id+"F51.imprint","IMPRINT",FACE,{"disambiguationData":[TD([[makeQuery(id+"F51.imprint","IMPRINT",EDGE,{"derivedFrom":sQuery(id+"F51.wireOp",EDGE,"E91")}),1.0]])]});
            extrude(context, id + "F52", {"entities" : qUnion([Q0, Q1]), "operationType" : NewBodyOperationType.REMOVE, "oppositeDirection" : true, "depth" : getVariable(context, 'headdepth'), "offsetDistance" : 25 * mm});
        }
    });
